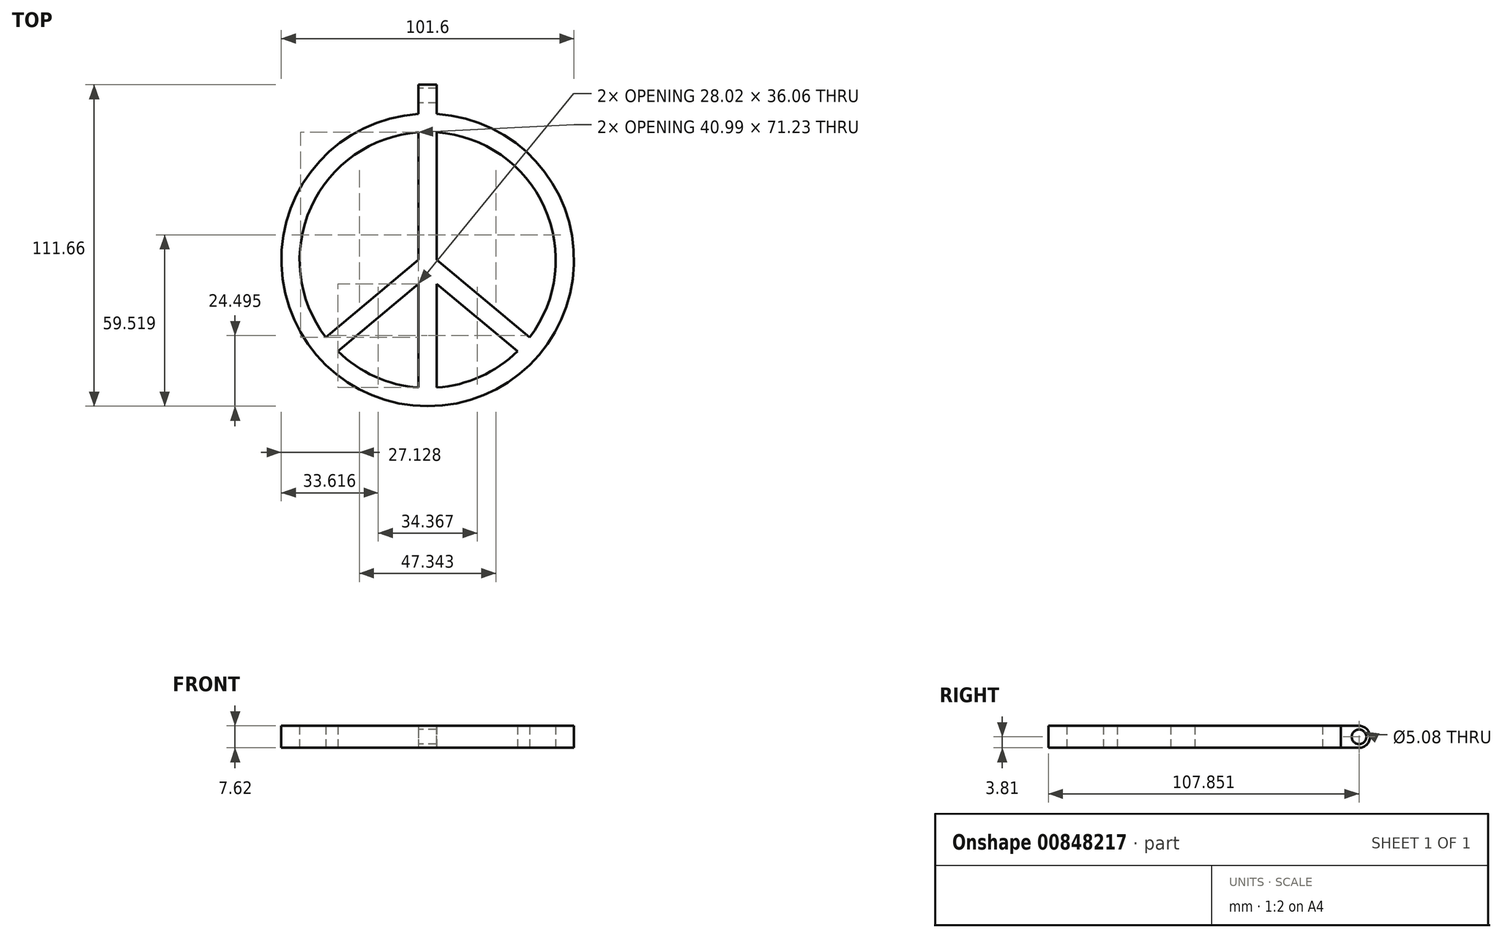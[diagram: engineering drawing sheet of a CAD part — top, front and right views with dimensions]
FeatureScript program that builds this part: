
annotation { "Feature Type Name" : "Feature", "Feature Type Description" : "" }
export const myFeature = defineFeature(function(context is Context, id is Id, definition is map)
    precondition{}
    {
        {
            var Q0;
            Q0=qCreatedBy(makeId("Top.planeOp"),FACE);
            var sketch = newSketch(context, id + "F0", { "sketchPlane" : qUnion([Q0])});
            skArc(sketch, "E0", {"start": v(-3.18, 50.7) * mm, "mid": v(0, -50.8) * mm, "end": v(3.18, 50.7) * mm});
            skArc(sketch, "E1", {"start": v(-3.18, 44.34) * mm, "mid": v(-40.5, 18.31) * mm, "end": v(-35.39, -26.9) * mm});
            skLineSegment(sketch, "E2.left", {"start": v(3.18, 44.34) * mm, "end": v(3.18, 0) * mm});
            skLineSegment(sketch, "E2.right", {"start": v(-3.18, 44.34) * mm, "end": v(-3.18, 0) * mm});
            skLineSegment(sketch, "E3", {"start": v(-3.18, 0) * mm, "end": v(-35.39, -26.9) * mm});
            skLineSegment(sketch, "E4", {"start": v(-3.18, -8.27) * mm, "end": v(-31.2, -31.67) * mm});
            skLineSegment(sketch, "E5.MirrorCS", {"start": v(3.18, 0) * mm, "end": v(35.39, -26.9) * mm});
            skLineSegment(sketch, "E6.MirrorCS", {"start": v(3.17, -8.27) * mm, "end": v(31.2, -31.67) * mm});
            skLineSegment(sketch, "E7.trimOffspring", {"start": v(-3.18, -8.27) * mm, "end": v(-3.18, -44.34) * mm});
            skLineSegment(sketch, "E8.trimOffspring", {"start": v(3.18, -8.27) * mm, "end": v(3.18, -44.34) * mm});
            skArc(sketch, "E9.trimOffspring", {"start": v(3.17, -44.34) * mm, "mid": v(18.31, -40.5) * mm, "end": v(31.2, -31.67) * mm});
            skArc(sketch, "E10.trimOffspring", {"start": v(-31.2, -31.67) * mm, "mid": v(-18.31, -40.5) * mm, "end": v(-3.18, -44.34) * mm});
            skArc(sketch, "E11.trimOffspring", {"start": v(35.39, -26.9) * mm, "mid": v(40.5, 18.31) * mm, "end": v(3.18, 44.34) * mm});
            skPoint(sketch, "E2.top.end.orphan", {"position": v(-3.18, -50.7) * mm});
            skPoint(sketch, "E2.top.start.orphan", {"position": v(3.18, -50.7) * mm});
            skPoint(sketch, "E2.bottom.end.orphan", {"position": v(-3.18, 50.7) * mm});
            skPoint(sketch, "E2.bottom.start.orphan", {"position": v(3.18, 50.7) * mm});
            skLineSegment(sketch, "E12", {"start": v(-3.18, 50.7) * mm, "end": v(-3.18, 60.86) * mm});
            skLineSegment(sketch, "E13", {"start": v(-3.18, 60.86) * mm, "end": v(3.18, 60.86) * mm});
            skLineSegment(sketch, "E14", {"start": v(3.18, 60.86) * mm, "end": v(3.18, 50.7) * mm});
            skSolve(sketch);
        }
        {
            var Q0;
            Q0 = qSketchRegion(id + "F0", true);
            extrude(context, id + "F1", {"entities" : qUnion([Q0]), "depth" : 7.62 * mm, "offsetDistance" : 25.4 * mm});
        }
        {
            var Q0;
            Q0=makeQuery(id+"F1.opExtrude","SWEPT_FACE",FACE,{"disambiguationData":[OSD([sQuery(id+"F0.wireOp",EDGE,"E12")])]});
            var sketch = newSketch(context, id + "F2", { "sketchPlane" : qUnion([Q0])});
            skCircle(sketch, "E15", {"center": v(-57.05, 3.81) * mm, "radius": 3.81 * mm});
            skPoint(sketch, "E15.centerSnap0", {"position": v(-50.7, 3.81) * mm});
            skCircle(sketch, "E16", {"center": v(-57.05, 3.81) * mm, "radius": 2.54 * mm});
            skLineSegment(sketch, "E17", {"start": v(-57.05, 0) * mm, "end": v(-60.86, 0) * mm});
            skLineSegment(sketch, "E18", {"start": v(-60.86, 0) * mm, "end": v(-60.86, 7.62) * mm});
            skLineSegment(sketch, "E19", {"start": v(-60.86, 7.62) * mm, "end": v(-57.05, 7.62) * mm});
            skSolve(sketch);
        }
        {
            var Q0;
            Q0=makeQuery(id+"F2.imprint","IMPRINT",FACE,{"disambiguationData":[TD([[makeQuery(id+"F2.imprint","IMPRINT",EDGE,{"derivedFrom":sQuery(id+"F2.wireOp",EDGE,"E16")}),1.0]])]});
            var Q1;
            {var subQ0=sQuery(id+"F2.wireOp",EDGE,"E19");Q1=makeQuery(id+"F2.imprint","IMPRINT",FACE,{"disambiguationData":[TD([[makeQuery(id+"F2.imprint","IMPRINT",EDGE,{"derivedFrom":subQ0}),1.0]])]});}
            var Q2;
            {var subQ0=sQuery(id+"F2.wireOp",EDGE,"E17");Q2=makeQuery(id+"F2.imprint","IMPRINT",FACE,{"disambiguationData":[TD([[makeQuery(id+"F2.imprint","IMPRINT",EDGE,{"derivedFrom":subQ0}),-1.0]])]});}
            extrude(context, id + "F3", {"entities" : qUnion([Q0, Q1, Q2]), "operationType" : NewBodyOperationType.REMOVE, "oppositeDirection" : true, "depth" : 25.4 * mm, "offsetDistance" : 25.4 * mm});
        }
    });
